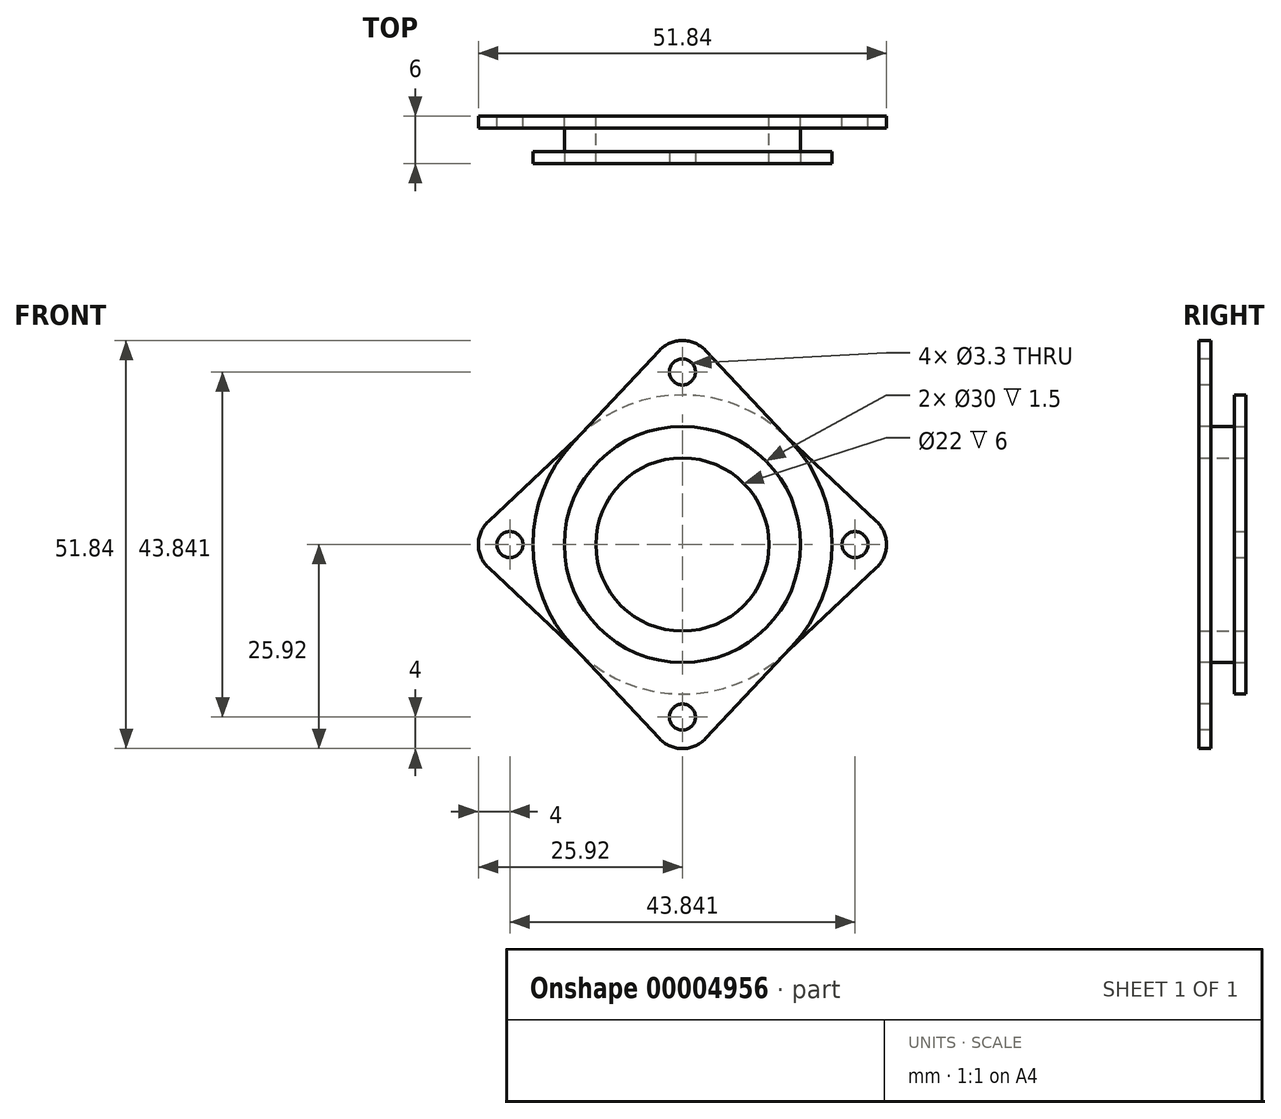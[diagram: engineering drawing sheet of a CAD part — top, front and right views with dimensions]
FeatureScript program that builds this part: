
annotation { "Feature Type Name" : "Feature", "Feature Type Description" : "" }
export const myFeature = defineFeature(function(context is Context, id is Id, definition is map)
    precondition{}
    {
        {
            var Q0;
            Q0=qCreatedBy(makeId("Front.planeOp"),FACE);
            var sketch = newSketch(context, id + "F0", { "sketchPlane" : qUnion([Q0])});
            skCircle(sketch, "E0", {"center": v(0, 0) * mm, "radius": 11 * mm});
            skCircle(sketch, "E1", {"center": v(0, 0) * mm, "radius": 15 * mm});
            skSolve(sketch);
        }
        {
            var Q0;
            Q0 = qSketchRegion(id + "F0", true);
            extrude(context, id + "F1", {"entities" : qUnion([Q0]), "depth" : 6 * mm, "symmetric" : true});
        }
        {
            var Q0;
            Q0=makeQuery(id+"F1.opExtrude","CAP_FACE",FACE,{"disambiguationData":[OSD([sQuery(id+"F0.wireOp",EDGE,"E0"),sQuery(id+"F0.wireOp",EDGE,"E1")])],"isStart":false});
            var sketch = newSketch(context, id + "F2", { "sketchPlane" : qUnion([Q0])});
            skCircle(sketch, "E2", {"center": v(0, 0) * mm, "radius": 19 * mm, "construction": true});
            skCircle(sketch, "E3", {"center": v(0, 0) * mm, "radius": 21.92 * mm, "construction": true});
            skLineSegment(sketch, "E4", {"start": v(0, 21.92) * mm, "end": v(0, 0) * mm, "construction": true});
            skLineSegment(sketch, "E5", {"start": v(0, 0) * mm, "end": v(21.92, 0) * mm, "construction": true});
            skCircle(sketch, "E6", {"center": v(0, 21.92) * mm, "radius": 1.65 * mm});
            skArc(sketch, "E7", {"start": v(2.92, 24.66) * mm, "mid": v(0, 25.92) * mm, "end": v(-2.92, 24.66) * mm});
            skArc(sketch, "E8", {"start": v(-13.85, 13) * mm, "mid": v(-19, 0) * mm, "end": v(-13.85, -13) * mm});
            skLineSegment(sketch, "E9", {"start": v(-2.92, 24.66) * mm, "end": v(-13.85, 13) * mm});
            skLineSegment(sketch, "E10.0.MirrorCS", {"start": v(-2.92, -24.66) * mm, "end": v(-13.85, -13) * mm});
            skCircle(sketch, "E11.0.MirrorC", {"center": v(0, -21.92) * mm, "radius": 1.65 * mm});
            skLineSegment(sketch, "E12.0.MirrorCS", {"start": v(2.92, -24.66) * mm, "end": v(13.85, -13) * mm});
            skLineSegment(sketch, "E12.1.MirrorCS", {"start": v(2.92, 24.66) * mm, "end": v(13.85, 13) * mm});
            skArc(sketch, "E13.0.MirrorCS", {"start": v(13.85, 13) * mm, "mid": v(19, 0) * mm, "end": v(13.85, -13) * mm});
            skArc(sketch, "E14.0.MirrorCS", {"start": v(2.92, -24.66) * mm, "mid": v(0, -25.92) * mm, "end": v(-2.92, -24.66) * mm});
            skCircle(sketch, "E15", {"center": v(0, 0) * mm, "radius": 15 * mm});
            skSolve(sketch);
        }
        {
            var Q0;
            Q0=makeQuery(id+"F2.imprint","IMPRINT",FACE,{"disambiguationData":[TD([[makeQuery(id+"F2.imprint","IMPRINT",EDGE,{"derivedFrom":sQuery(id+"F2.wireOp",EDGE,"E6")}),-1.0]])]});
            extrude(context, id + "F3", {"entities" : qUnion([Q0]), "oppositeDirection" : true, "depth" : 1.5 * mm});
        }
        {
            var Q0;
            Q0=makeQuery(id+"F1.opExtrude","CAP_FACE",FACE,{"disambiguationData":[OSD([sQuery(id+"F0.wireOp",EDGE,"E0"),sQuery(id+"F0.wireOp",EDGE,"E1")])],"isStart":true});
            var sketch = newSketch(context, id + "F4", { "sketchPlane" : qUnion([Q0])});
            skLineSegment(sketch, "E16", {"start": v(0, 0) * mm, "end": v(-21.92, 0) * mm, "construction": true});
            skLineSegment(sketch, "E17", {"start": v(0, 0) * mm, "end": v(0, 19.7) * mm, "construction": true});
            skCircle(sketch, "E18", {"center": v(-21.92, 0) * mm, "radius": 1.65 * mm});
            skArc(sketch, "E19", {"start": v(-24.66, 2.92) * mm, "mid": v(-25.92, 0) * mm, "end": v(-24.66, -2.92) * mm});
            skArc(sketch, "E20", {"start": v(13, 13.85) * mm, "mid": v(0, 19) * mm, "end": v(-13, 13.85) * mm});
            skLineSegment(sketch, "E21", {"start": v(-13, 13.85) * mm, "end": v(-24.66, 2.92) * mm});
            skCircle(sketch, "E22", {"center": v(0, 0) * mm, "radius": 15 * mm});
            skCircle(sketch, "E23.0.MirrorC", {"center": v(21.92, 0) * mm, "radius": 1.65 * mm});
            skLineSegment(sketch, "E23.1.MirrorCS", {"start": v(13, 13.85) * mm, "end": v(24.66, 2.92) * mm});
            skLineSegment(sketch, "E24.0.MirrorCS", {"start": v(13, -13.85) * mm, "end": v(24.66, -2.92) * mm});
            skArc(sketch, "E24.1.MirrorCS", {"start": v(13, -13.85) * mm, "mid": v(0, -19) * mm, "end": v(-13, -13.85) * mm});
            skLineSegment(sketch, "E24.2.MirrorCS", {"start": v(-13, -13.85) * mm, "end": v(-24.66, -2.92) * mm});
            skArc(sketch, "E25.0.MirrorCS", {"start": v(24.66, 2.92) * mm, "mid": v(25.92, 0) * mm, "end": v(24.66, -2.92) * mm});
            skSolve(sketch);
        }
        {
            var Q0;
            Q0=makeQuery(id+"F4.imprint","IMPRINT",FACE,{"disambiguationData":[TD([[makeQuery(id+"F4.imprint","IMPRINT",EDGE,{"derivedFrom":sQuery(id+"F4.wireOp",EDGE,"E18")}),-1.0]])]});
            extrude(context, id + "F5", {"entities" : qUnion([Q0]), "oppositeDirection" : true, "depth" : 1.5 * mm});
        }
    });
